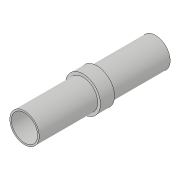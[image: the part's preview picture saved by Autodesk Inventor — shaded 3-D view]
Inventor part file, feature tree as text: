
AUTODESK INVENTOR PART (.ipt)
format: ipt  version: 2018.3 (Build 223284000, 284)  size: 99,328 bytes
history: native  units: in
note: dims shown in document units (in); Inventor stores cm internally (conversion verified against a paired STEP export)
features: extrude x4, sketch x4
ambient origin geometry x8: Origin, YZ Plane, XZ Plane, XY Plane, X Axis, Y Axis, Z Axis, Center Point
bodies: Solid1 (feature_tree)
feature tree (8):
  extrude  "Extrusion1"  Depth=1.87in TaperAngle=0.0deg
  extrude  "Extrusion2"  Depth=0.835in TaperAngle=0.0deg
  extrude  "Extrusion3"  Depth=0.835in TaperAngle=0.0deg
  extrude  "Extrusion4"  Depth=0.835in TaperAngle=0.0deg
  sketch  "Sketch1"  dims[d0=0.5in d2=1.87in d3=0.0in]
  sketch  "Sketch2"  dims[d4=0.42in d5=0.835in d6=0.0in]
  sketch  "Sketch3"  dims[d7=0.42in d8=0.835in d9=0.0in]
  sketch  "Sketch4"  dims[d10=0.375in d11=0.835in d12=0.0in]
